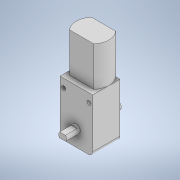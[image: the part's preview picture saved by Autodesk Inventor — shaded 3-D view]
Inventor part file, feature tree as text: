
AUTODESK INVENTOR PART (.ipt)
format: ipt  version: 2020 (Build 240168000, 168)  size: 182,272 bytes
history: native  units: mm
features: extrude x7, sketch x7, mirror x1, fillet x1
ambient origin geometry x8: Origin, YZ Plane, XZ Plane, XY Plane, X Axis, Y Axis, Z Axis, Center Point
bodies: Solid1 (feature_tree)
feature tree (16):
  extrude  "Extrusion1"  Depth=18.8mm
  extrude  "Extrusion2"  Depth=37.0mm
  extrude  "Extrusion3"  Depth=9.5mm TaperAngle=0.0deg
  mirror  "Mirror1"
  extrude  "Extrusion4"  Depth=7.9mm TaperAngle=0.0deg
  extrude  "Extrusion5"  Depth=3.0mm
  extrude  "Extrusion6"  Depth=5.0mm
  extrude  "Extrusion7"  Depth=5.0mm TaperAngle=0.0deg
  fillet  "Fillet1"  Radius=3.7mm
  sketch  "Sketch1"  dims[d0=22.5mm d1=18.8mm]
  sketch  "Sketch2"  dims[d2=37.0mm d3=0.0mm d4=5.4mm]
  sketch  "Sketch3"  dims[d5=11.2mm d6=9.5mm d7=0.0mm]
  sketch  "Sketch4"  dims[d8=3.6mm d9=7.9mm d10=0.0mm]
  sketch  "Sketch5"  dims[d11=5.0mm d12=3.0mm]
  sketch  "Sketch6"  dims[d13=5.0mm d14=0.0mm d15=2.8mm]
  sketch  "Sketch7"  dims[d16=2.4mm d17=5.0mm d18=0.0mm d19=3.7mm d20=27.2mm d21=0.0mm d22=10.8mm d23=15.1mm d24=7.55mm d25=2.8mm d26=31.1mm d27=20.0mm d29=17.5mm d30=10.0mm d32=10.0mm d34=22.5mm d35=2.5mm d36=4.0mm d37=0.0mm d38=3.0mm]
